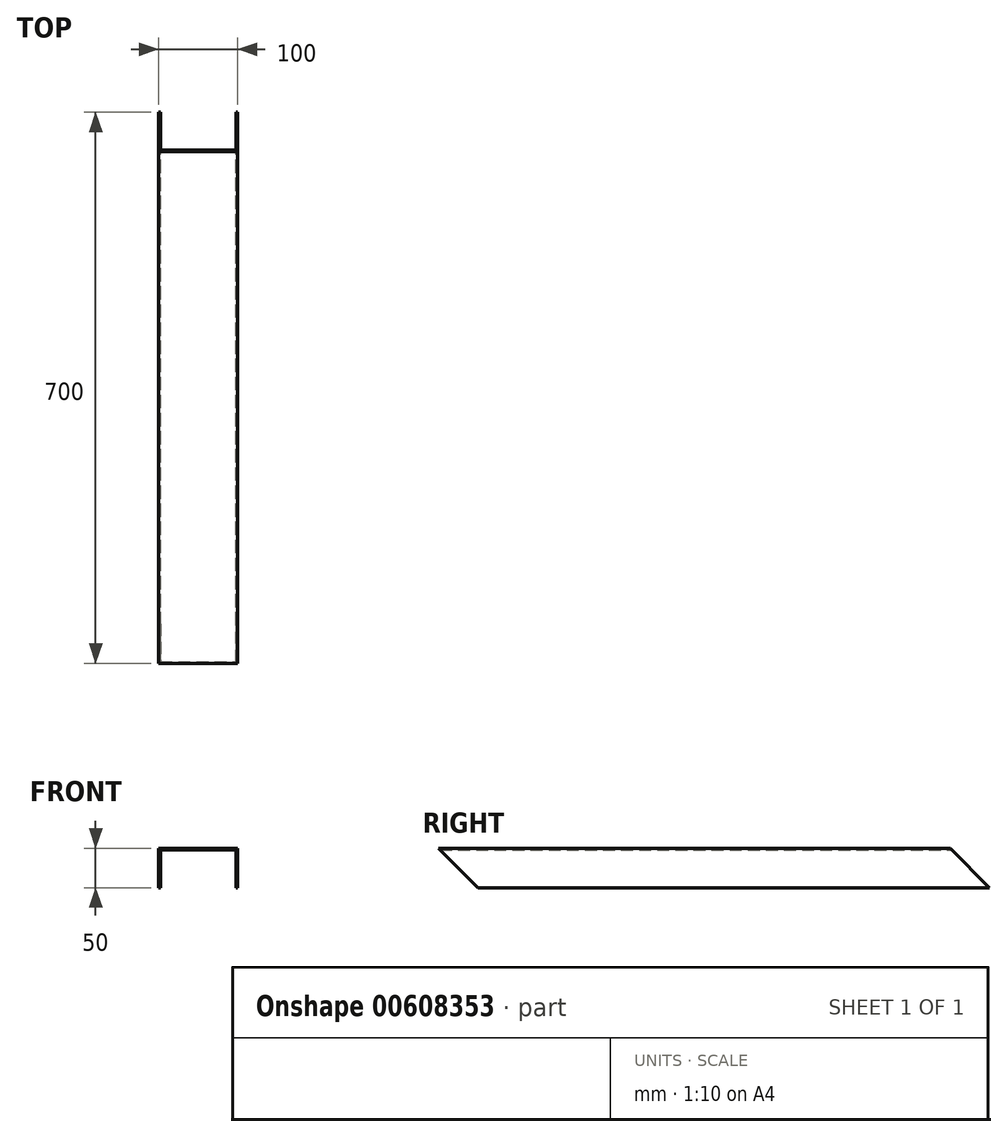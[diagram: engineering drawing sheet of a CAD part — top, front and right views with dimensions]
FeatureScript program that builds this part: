
annotation { "Feature Type Name" : "Feature", "Feature Type Description" : "" }
export const myFeature = defineFeature(function(context is Context, id is Id, definition is map)
    precondition{}
    {
        {
            var Q0;
            Q0=qCreatedBy(makeId("Front.planeOp"),FACE);
            var sketch = newSketch(context, id + "F0", { "sketchPlane" : qUnion([Q0])});
            skLineSegment(sketch, "E0", {"start": v(0, 28.89) * mm, "end": v(-50, 28.89) * mm});
            skLineSegment(sketch, "E1", {"start": v(-50, 28.89) * mm, "end": v(-50, -21.11) * mm});
            skLineSegment(sketch, "E2", {"start": v(-50, -21.11) * mm, "end": v(-48, -21.11) * mm});
            skLineSegment(sketch, "E3", {"start": v(-48, -21.11) * mm, "end": v(-48, 26.89) * mm});
            skLineSegment(sketch, "E4", {"start": v(-48, 26.89) * mm, "end": v(0, 26.89) * mm});
            skLineSegment(sketch, "E5.MirrorCS", {"start": v(48, 26.89) * mm, "end": v(0, 26.89) * mm});
            skLineSegment(sketch, "E6.MirrorCS", {"start": v(0, 28.89) * mm, "end": v(50, 28.89) * mm});
            skLineSegment(sketch, "E7.MirrorCS", {"start": v(48, -21.11) * mm, "end": v(48, 26.89) * mm});
            skLineSegment(sketch, "E8.MirrorCS", {"start": v(50, 28.89) * mm, "end": v(50, -21.11) * mm});
            skLineSegment(sketch, "E9.MirrorCS", {"start": v(50, -21.11) * mm, "end": v(48, -21.11) * mm});
            skSolve(sketch);
        }
        {
            var Q0;
            Q0=makeQuery(id+"F0.imprint","IMPRINT",FACE,{"disambiguationData":[TD([[makeQuery(id+"F0.imprint","IMPRINT",EDGE,{"derivedFrom":sQuery(id+"F0.wireOp",EDGE,"E0")}),1.0]])]});
            extrude(context, id + "F1", {"entities" : qUnion([Q0]), "endBound" : BoundingType.SYMMETRIC, "depth" : 700 * mm, "offsetDistance" : 25 * mm});
        }
        {
            var Q0;
            Q0=makeQuery(id+"F1.opExtrude","SWEPT_FACE",FACE,{"disambiguationData":[OSD([sQuery(id+"F0.wireOp",EDGE,"E8.MirrorCS")])]});
            var sketch = newSketch(context, id + "F2", { "sketchPlane" : qUnion([Q0])});
            skLineSegment(sketch, "E10", {"start": v(-350, 28.89) * mm, "end": v(-300, -21.11) * mm});
            skLineSegment(sketch, "E11", {"start": v(350, -21.11) * mm, "end": v(300, 28.89) * mm});
            skSolve(sketch);
        }
        {
            var Q0;
            {var subQ0=sQuery(id+"F2.wireOp",EDGE,"E10");Q0=makeQuery(id+"F2.imprint","IMPRINT",FACE,{"disambiguationData":[TD([[makeQuery(id+"F2.imprint","IMPRINT",EDGE,{"derivedFrom":subQ0}),-1.0]])]});}
            var Q1;
            {var subQ0=sQuery(id+"F2.wireOp",EDGE,"E11");Q1=makeQuery(id+"F2.imprint","IMPRINT",FACE,{"disambiguationData":[TD([[makeQuery(id+"F2.imprint","IMPRINT",EDGE,{"derivedFrom":subQ0}),-1.0]])]});}
            extrude(context, id + "F3", {"entities" : qUnion([Q0, Q1]), "operationType" : NewBodyOperationType.REMOVE, "endBound" : BoundingType.THROUGH_ALL, "oppositeDirection" : true, "depth" : 25 * mm, "offsetDistance" : 25 * mm});
        }
    });
